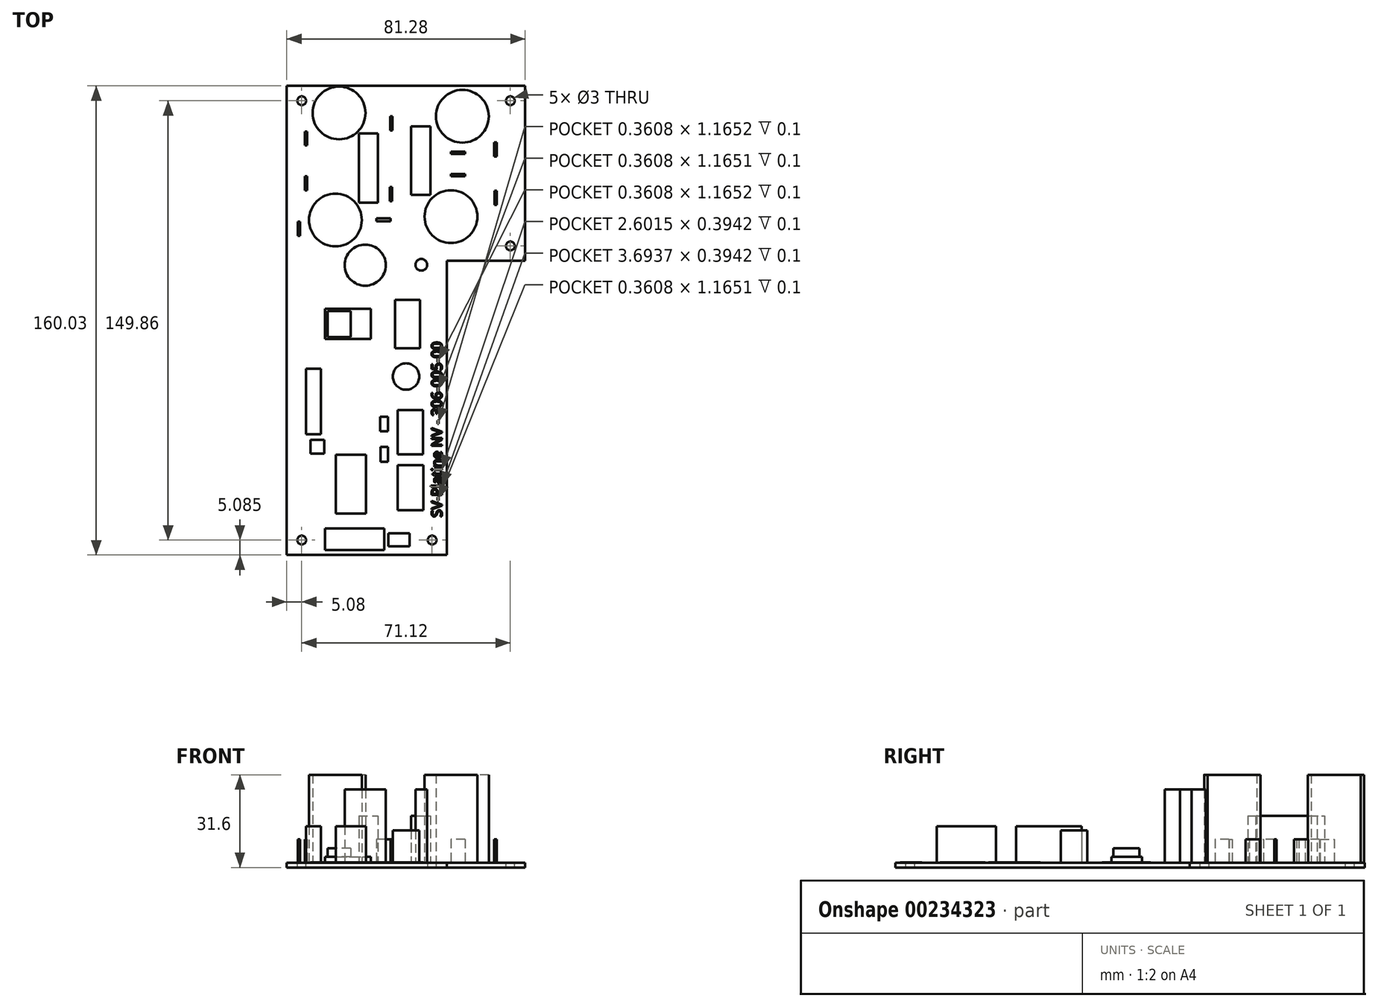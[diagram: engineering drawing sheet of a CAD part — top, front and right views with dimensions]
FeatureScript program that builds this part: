
annotation { "Feature Type Name" : "Feature", "Feature Type Description" : "" }
export const myFeature = defineFeature(function(context is Context, id is Id, definition is map)
    precondition{}
    {
        {
            var Q0;
            Q0=qCreatedBy(makeId("Top.planeOp"),FACE);
            var sketch = newSketch(context, id + "F0", { "sketchPlane" : qUnion([Q0])});
            skLineSegment(sketch, "E0.bottom", {"start": v(40.64, -29.84) * mm, "end": v(13.97, -29.84) * mm});
            skLineSegment(sketch, "E0.top", {"start": v(40.64, 29.85) * mm, "end": v(-40.64, 29.85) * mm});
            skLineSegment(sketch, "E0.left", {"start": v(40.64, -29.84) * mm, "end": v(40.64, 29.85) * mm});
            skLineSegment(sketch, "E0.right", {"start": v(-40.64, -29.84) * mm, "end": v(-40.64, 29.85) * mm});
            skPoint(sketch, "E0.middle", {"position": v(0, 0) * mm});
            skCircle(sketch, "E1.MirrorC", {"center": v(35.56, -24.76) * mm, "radius": 1.5 * mm});
            skCircle(sketch, "E2.MirrorC", {"center": v(-35.56, 24.77) * mm, "radius": 1.5 * mm});
            skCircle(sketch, "E3.MirrorC", {"center": v(35.56, 24.76) * mm, "radius": 1.5 * mm});
            skLineSegment(sketch, "E4.top", {"start": v(-40.64, -130.18) * mm, "end": v(13.97, -130.18) * mm});
            skLineSegment(sketch, "E4.left", {"start": v(-40.64, -29.84) * mm, "end": v(-40.64, -130.18) * mm});
            skLineSegment(sketch, "E4.right", {"start": v(13.97, -29.84) * mm, "end": v(13.97, -130.18) * mm});
            skCircle(sketch, "E5.MirrorC", {"center": v(-35.56, -125.1) * mm, "radius": 1.5 * mm});
            skCircle(sketch, "E6", {"center": v(8.89, -125.1) * mm, "radius": 1.5 * mm});
            skSolve(sketch);
        }
        {
            var Q0;
            Q0=makeQuery(id+"F0.imprint","IMPRINT",FACE,{"disambiguationData":[TD([[makeQuery(id+"F0.imprint","IMPRINT",EDGE,{"derivedFrom":sQuery(id+"F0.wireOp",EDGE,"Te7iasoo-ddtE-R7LS-BblS-gFD69E2wKtYx")}),-1.0]])]});
            var Q1;
            Q1=makeQuery(id+"F0.imprint","IMPRINT",FACE,{"disambiguationData":[TD([[makeQuery(id+"F0.imprint","IMPRINT",EDGE,{"derivedFrom":sQuery(id+"F0.wireOp",EDGE,"E4.bottom")}),-1.0]])]});
            var Q2;
            Q2=makeQuery(id+"F0.imprint","IMPRINT",FACE,{"disambiguationData":[TD([[makeQuery(id+"F0.imprint","IMPRINT",EDGE,{"derivedFrom":sQuery(id+"F0.wireOp",EDGE,"E0.bottom")}),-1.0]])]});
            extrude(context, id + "F1", {"entities" : qUnion([Q0, Q1, Q2]), "oppositeDirection" : true, "depth" : 1.6 * mm, "offsetDistance" : 25 * mm});
        }
        {
            var Q0;
            Q0=makeQuery(id+"F1.opExtrude","CAP_FACE",FACE,{"disambiguationData":[OSD([sQuery(id+"F0.wireOp",EDGE,"E0.bottom"),sQuery(id+"F0.wireOp",EDGE,"E0.top"),sQuery(id+"F0.wireOp",EDGE,"E0.left"),sQuery(id+"F0.wireOp",EDGE,"E0.right"),sQuery(id+"F0.wireOp",EDGE,"E1.MirrorC"),sQuery(id+"F0.wireOp",EDGE,"E2.MirrorC"),sQuery(id+"F0.wireOp",EDGE,"E3.MirrorC"),sQuery(id+"F0.wireOp",EDGE,"E4.top"),sQuery(id+"F0.wireOp",EDGE,"E4.left"),sQuery(id+"F0.wireOp",EDGE,"E4.right"),sQuery(id+"F0.wireOp",EDGE,"E5.MirrorC")])],"isStart":true});
            var sketch = newSketch(context, id + "F2", { "sketchPlane" : qUnion([Q0])});
            skText(sketch, "E7", { "text": "SV-Platine NV - 306-005-00", "fontName": "OpenSans-Regular.ttf"});
            const initialGuessF2  = {"E7": [0.0122, -0.11735, 0, 1, 0.0035]};
            skSetInitialGuess(sketch, initialGuessF2);
            skSolve(sketch);
        }
        {
            var Q0;
            Q0 = qSketchRegion(id + "F2", true);
            extrude(context, id + "F3", {"entities" : qUnion([Q0]), "operationType" : NewBodyOperationType.REMOVE, "oppositeDirection" : true, "depth" : .1 * mm, "offsetDistance" : 25 * mm});
        }
        {
            var Q0;
            {var subQ0=sQuery(id+"F0.wireOp",EDGE,"E4.right");var subQ1=sQuery(id+"F0.wireOp",EDGE,"E4.top");var subQ2=sQuery(id+"F0.wireOp",EDGE,"E3.MirrorC");var subQ3=sQuery(id+"F0.wireOp",EDGE,"E2.MirrorC");var subQ4=sQuery(id+"F0.wireOp",EDGE,"E1.MirrorC");var subQ5=sQuery(id+"F0.wireOp",EDGE,"E5.MirrorC");var subQ6=sQuery(id+"F0.wireOp",EDGE,"E0.bottom");var subQ7=sQuery(id+"F0.wireOp",EDGE,"E4.left");var subQ8=sQuery(id+"F0.wireOp",EDGE,"E0.right");var subQ9=sQuery(id+"F0.wireOp",EDGE,"E0.top");var subQ10=sQuery(id+"F0.wireOp",EDGE,"E0.left");var subQ11=sQuery(id+"F0.wireOp",EDGE,"E6");Q0=makeQuery(id+"F3.boolean.opBoolean","SPLIT",FACE,{"disambiguationData":[TD([makeQuery(id+"F1.opExtrude","SWEPT_FACE",FACE,{"disambiguationData":[OSD([subQ6])]})])],"derivedFrom":makeQuery(id+"F1.opExtrude","CAP_FACE",FACE,{"disambiguationData":[OSD([subQ6,subQ9,subQ10,subQ8,subQ4,subQ3,subQ2,subQ1,subQ7,subQ0,subQ5,subQ11])],"isStart":true})});}
            var sketch = newSketch(context, id + "F4", { "sketchPlane" : qUnion([Q0])});
            skCircle(sketch, "E8", {"center": v(-24.07, -15.93) * mm, "radius": 9 * mm});
            skCircle(sketch, "E9", {"center": v(-22.82, 20.6) * mm, "radius": 9 * mm});
            skCircle(sketch, "E10", {"center": v(15.31, -14.76) * mm, "radius": 9 * mm});
            skCircle(sketch, "E11", {"center": v(19.21, 19.47) * mm, "radius": 9 * mm});
            skCircle(sketch, "E12", {"center": v(-13.91, -31.32) * mm, "radius": 7 * mm});
            skCircle(sketch, "E13", {"center": v(-26.64, -61.49) * mm, "radius": 3 * mm});
            skCircle(sketch, "E14", {"center": v(0, -69.3) * mm, "radius": 4.5 * mm});
            skLineSegment(sketch, "E15.bottom", {"start": v(-27.68, -56.55) * mm, "end": v(-11.95, -56.55) * mm});
            skLineSegment(sketch, "E15.top", {"start": v(-27.68, -46.15) * mm, "end": v(-11.95, -46.15) * mm});
            skLineSegment(sketch, "E15.left", {"start": v(-27.68, -56.55) * mm, "end": v(-27.68, -46.15) * mm});
            skLineSegment(sketch, "E15.right", {"start": v(-11.95, -56.55) * mm, "end": v(-11.95, -46.15) * mm});
            skLineSegment(sketch, "E16.bottom", {"start": v(-18.88, -46.95) * mm, "end": v(-26.79, -46.95) * mm});
            skLineSegment(sketch, "E16.top", {"start": v(-18.88, -55.84) * mm, "end": v(-26.79, -55.84) * mm});
            skLineSegment(sketch, "E16.left", {"start": v(-18.88, -46.95) * mm, "end": v(-18.88, -55.84) * mm});
            skLineSegment(sketch, "E16.right", {"start": v(-26.79, -46.95) * mm, "end": v(-26.79, -55.84) * mm});
            skLineSegment(sketch, "E17.bottom", {"start": v(-3.71, -59.64) * mm, "end": v(4.76, -59.64) * mm});
            skLineSegment(sketch, "E17.top", {"start": v(-3.71, -43.2) * mm, "end": v(4.76, -43.2) * mm});
            skLineSegment(sketch, "E17.left", {"start": v(-3.71, -59.64) * mm, "end": v(-3.71, -43.2) * mm});
            skLineSegment(sketch, "E17.right", {"start": v(4.76, -59.64) * mm, "end": v(4.76, -43.2) * mm});
            skLineSegment(sketch, "E18.bottom", {"start": v(-2.88, -95.85) * mm, "end": v(5.83, -95.85) * mm});
            skLineSegment(sketch, "E18.top", {"start": v(-2.88, -80.74) * mm, "end": v(5.83, -80.74) * mm});
            skLineSegment(sketch, "E18.left", {"start": v(-2.88, -95.85) * mm, "end": v(-2.88, -80.74) * mm});
            skLineSegment(sketch, "E18.right", {"start": v(5.83, -95.85) * mm, "end": v(5.83, -80.74) * mm});
            skLineSegment(sketch, "E19.bottom", {"start": v(-2.88, -114.87) * mm, "end": v(5.92, -114.87) * mm});
            skLineSegment(sketch, "E19.top", {"start": v(-2.88, -99.58) * mm, "end": v(5.92, -99.58) * mm});
            skLineSegment(sketch, "E19.left", {"start": v(-2.88, -114.87) * mm, "end": v(-2.88, -99.58) * mm});
            skLineSegment(sketch, "E19.right", {"start": v(5.92, -114.87) * mm, "end": v(5.92, -99.58) * mm});
            skLineSegment(sketch, "E20.bottom", {"start": v(-27.68, -128.52) * mm, "end": v(-7.41, -128.52) * mm});
            skLineSegment(sketch, "E20.top", {"start": v(-27.68, -121.14) * mm, "end": v(-7.41, -121.14) * mm});
            skLineSegment(sketch, "E20.left", {"start": v(-27.68, -128.52) * mm, "end": v(-27.68, -121.14) * mm});
            skLineSegment(sketch, "E20.right", {"start": v(-7.41, -128.52) * mm, "end": v(-7.41, -121.14) * mm});
            skLineSegment(sketch, "E21.bottom", {"start": v(-6, -127.28) * mm, "end": v(1.2, -127.28) * mm});
            skLineSegment(sketch, "E21.top", {"start": v(-6, -122.74) * mm, "end": v(1.2, -122.74) * mm});
            skLineSegment(sketch, "E21.left", {"start": v(-6, -127.28) * mm, "end": v(-6, -122.74) * mm});
            skLineSegment(sketch, "E21.right", {"start": v(1.2, -127.28) * mm, "end": v(1.2, -122.74) * mm});
            skLineSegment(sketch, "E22.bottom", {"start": v(-34.04, -88.97) * mm, "end": v(-29.08, -88.97) * mm});
            skLineSegment(sketch, "E22.top", {"start": v(-34.04, -66.69) * mm, "end": v(-29.08, -66.69) * mm});
            skLineSegment(sketch, "E22.left", {"start": v(-34.04, -88.97) * mm, "end": v(-34.04, -66.69) * mm});
            skLineSegment(sketch, "E22.right", {"start": v(-29.08, -88.97) * mm, "end": v(-29.08, -66.69) * mm});
            skLineSegment(sketch, "E23.bottom", {"start": v(-23.94, -116.1) * mm, "end": v(-13.63, -116.1) * mm});
            skLineSegment(sketch, "E23.top", {"start": v(-23.94, -95.92) * mm, "end": v(-13.63, -95.92) * mm});
            skLineSegment(sketch, "E23.left", {"start": v(-23.94, -116.1) * mm, "end": v(-23.94, -95.92) * mm});
            skLineSegment(sketch, "E23.right", {"start": v(-13.63, -116.1) * mm, "end": v(-13.63, -95.92) * mm});
            skLineSegment(sketch, "E24.bottom", {"start": v(-8.75, -98.41) * mm, "end": v(-6.17, -98.41) * mm});
            skLineSegment(sketch, "E24.top", {"start": v(-8.75, -93.26) * mm, "end": v(-6.17, -93.26) * mm});
            skLineSegment(sketch, "E24.left", {"start": v(-8.75, -98.41) * mm, "end": v(-8.75, -93.26) * mm});
            skLineSegment(sketch, "E24.right", {"start": v(-6.17, -98.41) * mm, "end": v(-6.17, -93.26) * mm});
            skLineSegment(sketch, "E25.bottom", {"start": v(-8.76, -88.03) * mm, "end": v(-6.17, -88.03) * mm});
            skLineSegment(sketch, "E25.top", {"start": v(-8.76, -83.06) * mm, "end": v(-6.17, -83.06) * mm});
            skLineSegment(sketch, "E25.left", {"start": v(-8.76, -88.03) * mm, "end": v(-8.76, -83.06) * mm});
            skLineSegment(sketch, "E25.right", {"start": v(-6.17, -88.03) * mm, "end": v(-6.17, -83.06) * mm});
            skLineSegment(sketch, "E26.bottom", {"start": v(-16.12, -10.04) * mm, "end": v(-9.55, -10.04) * mm});
            skLineSegment(sketch, "E26.top", {"start": v(-16.12, 13.6) * mm, "end": v(-9.55, 13.6) * mm});
            skLineSegment(sketch, "E26.left", {"start": v(-16.12, -10.04) * mm, "end": v(-16.12, 13.6) * mm});
            skLineSegment(sketch, "E26.right", {"start": v(-9.55, -10.04) * mm, "end": v(-9.55, 13.6) * mm});
            skLineSegment(sketch, "E27.bottom", {"start": v(1.65, -7.38) * mm, "end": v(8.32, -7.38) * mm});
            skLineSegment(sketch, "E27.top", {"start": v(1.65, 16.09) * mm, "end": v(8.32, 16.09) * mm});
            skLineSegment(sketch, "E27.left", {"start": v(1.65, -7.38) * mm, "end": v(1.65, 16.09) * mm});
            skLineSegment(sketch, "E27.right", {"start": v(8.32, -7.38) * mm, "end": v(8.32, 16.09) * mm});
            skCircle(sketch, "E28", {"center": v(5.2, -31.2) * mm, "radius": 2 * mm});
            skLineSegment(sketch, "E29.bottom", {"start": v(-34.5, 14.31) * mm, "end": v(-33.7, 14.31) * mm});
            skLineSegment(sketch, "E29.top", {"start": v(-34.5, 9.51) * mm, "end": v(-33.7, 9.51) * mm});
            skLineSegment(sketch, "E29.left", {"start": v(-34.5, 14.31) * mm, "end": v(-34.5, 9.51) * mm});
            skLineSegment(sketch, "E29.right", {"start": v(-33.7, 14.31) * mm, "end": v(-33.7, 9.51) * mm});
            skLineSegment(sketch, "E30.bottom", {"start": v(-34.5, -0.96) * mm, "end": v(-33.7, -0.96) * mm});
            skLineSegment(sketch, "E30.top", {"start": v(-34.5, -5.76) * mm, "end": v(-33.7, -5.76) * mm});
            skLineSegment(sketch, "E30.left", {"start": v(-34.5, -0.96) * mm, "end": v(-34.5, -5.76) * mm});
            skLineSegment(sketch, "E30.right", {"start": v(-33.7, -0.96) * mm, "end": v(-33.7, -5.76) * mm});
            skLineSegment(sketch, "E31.bottom", {"start": v(-36.9, -16.45) * mm, "end": v(-36.1, -16.45) * mm});
            skLineSegment(sketch, "E31.top", {"start": v(-36.9, -21.25) * mm, "end": v(-36.1, -21.25) * mm});
            skLineSegment(sketch, "E31.left", {"start": v(-36.9, -16.45) * mm, "end": v(-36.9, -21.25) * mm});
            skLineSegment(sketch, "E31.right", {"start": v(-36.1, -16.45) * mm, "end": v(-36.1, -21.25) * mm});
            skLineSegment(sketch, "E32.bottom", {"start": v(-32.58, -90.9) * mm, "end": v(-27.92, -90.9) * mm});
            skLineSegment(sketch, "E32.top", {"start": v(-32.58, -95.62) * mm, "end": v(-27.92, -95.62) * mm});
            skLineSegment(sketch, "E32.left", {"start": v(-32.58, -90.9) * mm, "end": v(-32.58, -95.62) * mm});
            skLineSegment(sketch, "E32.right", {"start": v(-27.92, -90.9) * mm, "end": v(-27.92, -95.62) * mm});
            skLineSegment(sketch, "E33.bottom", {"start": v(-4.64, 14.65) * mm, "end": v(-5.44, 14.65) * mm});
            skLineSegment(sketch, "E33.top", {"start": v(-4.64, 19.45) * mm, "end": v(-5.44, 19.45) * mm});
            skLineSegment(sketch, "E33.left", {"start": v(-4.64, 14.65) * mm, "end": v(-4.64, 19.45) * mm});
            skLineSegment(sketch, "E33.right", {"start": v(-5.44, 14.65) * mm, "end": v(-5.44, 19.45) * mm});
            skPoint(sketch, "E33.middle", {"position": v(-5.04, 17.05) * mm});
            skLineSegment(sketch, "E34.bottom", {"start": v(-4.71, -9.51) * mm, "end": v(-5.51, -9.51) * mm});
            skLineSegment(sketch, "E34.top", {"start": v(-4.71, -4.71) * mm, "end": v(-5.51, -4.71) * mm});
            skLineSegment(sketch, "E34.left", {"start": v(-4.71, -9.51) * mm, "end": v(-4.71, -4.71) * mm});
            skLineSegment(sketch, "E34.right", {"start": v(-5.51, -9.51) * mm, "end": v(-5.51, -4.71) * mm});
            skPoint(sketch, "E34.middle", {"position": v(-5.11, -7.11) * mm});
            skLineSegment(sketch, "E35.bottom", {"start": v(-5.28, -16.42) * mm, "end": v(-10.08, -16.42) * mm});
            skLineSegment(sketch, "E35.top", {"start": v(-5.28, -15.37) * mm, "end": v(-10.08, -15.37) * mm});
            skLineSegment(sketch, "E35.left", {"start": v(-5.28, -16.42) * mm, "end": v(-5.28, -15.37) * mm});
            skLineSegment(sketch, "E35.right", {"start": v(-10.08, -16.42) * mm, "end": v(-10.08, -15.37) * mm});
            skPoint(sketch, "E35.middle", {"position": v(-7.68, -15.9) * mm});
            skLineSegment(sketch, "E36.bottom", {"start": v(20.16, -1.01) * mm, "end": v(15.36, -1.01) * mm});
            skLineSegment(sketch, "E36.top", {"start": v(20.16, -0.21) * mm, "end": v(15.36, -0.21) * mm});
            skLineSegment(sketch, "E36.left", {"start": v(20.16, -1.01) * mm, "end": v(20.16, -0.21) * mm});
            skLineSegment(sketch, "E36.right", {"start": v(15.36, -1.01) * mm, "end": v(15.36, -0.21) * mm});
            skPoint(sketch, "E36.middle", {"position": v(17.76, -0.61) * mm});
            skLineSegment(sketch, "E37.bottom", {"start": v(20.1, 6.57) * mm, "end": v(15.3, 6.57) * mm});
            skLineSegment(sketch, "E37.top", {"start": v(20.1, 7.37) * mm, "end": v(15.3, 7.37) * mm});
            skLineSegment(sketch, "E37.left", {"start": v(20.1, 6.57) * mm, "end": v(20.1, 7.37) * mm});
            skLineSegment(sketch, "E37.right", {"start": v(15.3, 6.57) * mm, "end": v(15.3, 7.37) * mm});
            skPoint(sketch, "E37.middle", {"position": v(17.7, 6.97) * mm});
            skLineSegment(sketch, "E38.bottom", {"start": v(30.87, 5.76) * mm, "end": v(30.07, 5.76) * mm});
            skLineSegment(sketch, "E38.top", {"start": v(30.87, 10.56) * mm, "end": v(30.07, 10.56) * mm});
            skLineSegment(sketch, "E38.left", {"start": v(30.87, 5.76) * mm, "end": v(30.87, 10.56) * mm});
            skLineSegment(sketch, "E38.right", {"start": v(30.07, 5.76) * mm, "end": v(30.07, 10.56) * mm});
            skPoint(sketch, "E38.middle", {"position": v(30.47, 8.16) * mm});
            skLineSegment(sketch, "E39.bottom", {"start": v(30.9, -10.75) * mm, "end": v(30.1, -10.75) * mm});
            skLineSegment(sketch, "E39.top", {"start": v(30.9, -5.95) * mm, "end": v(30.1, -5.95) * mm});
            skLineSegment(sketch, "E39.left", {"start": v(30.9, -10.75) * mm, "end": v(30.9, -5.95) * mm});
            skLineSegment(sketch, "E39.right", {"start": v(30.1, -10.75) * mm, "end": v(30.1, -5.95) * mm});
            skPoint(sketch, "E39.middle", {"position": v(30.5, -8.35) * mm});
            skSolve(sketch);
        }
        {
            var Q0;
            Q0=makeQuery(id+"F4.imprint","IMPRINT",FACE,{"disambiguationData":[TD([[makeQuery(id+"F4.imprint","IMPRINT",EDGE,{"derivedFrom":sQuery(id+"F4.wireOp",EDGE,"E11")}),1.0]])]});
            var Q1;
            Q1=makeQuery(id+"F4.imprint","IMPRINT",FACE,{"disambiguationData":[TD([[makeQuery(id+"F4.imprint","IMPRINT",EDGE,{"derivedFrom":sQuery(id+"F4.wireOp",EDGE,"E9")}),1.0]])]});
            var Q2;
            Q2=makeQuery(id+"F4.imprint","IMPRINT",FACE,{"disambiguationData":[TD([[makeQuery(id+"F4.imprint","IMPRINT",EDGE,{"derivedFrom":sQuery(id+"F4.wireOp",EDGE,"E8")}),1.0]])]});
            var Q3;
            Q3=makeQuery(id+"F4.imprint","IMPRINT",FACE,{"disambiguationData":[TD([[makeQuery(id+"F4.imprint","IMPRINT",EDGE,{"derivedFrom":sQuery(id+"F4.wireOp",EDGE,"E10")}),1.0]])]});
            extrude(context, id + "F5", {"entities" : qUnion([Q0, Q1, Q2, Q3]), "operationType" : NewBodyOperationType.ADD, "depth" : 30 * mm, "offsetDistance" : 25 * mm});
        }
        {
            var Q0;
            Q0=makeQuery(id+"F4.imprint","IMPRINT",FACE,{"disambiguationData":[TD([[makeQuery(id+"F4.imprint","IMPRINT",EDGE,{"derivedFrom":sQuery(id+"F4.wireOp",EDGE,"E12")}),1.0]])]});
            extrude(context, id + "F6", {"entities" : qUnion([Q0]), "operationType" : NewBodyOperationType.ADD, "depth" : 25 * mm, "offsetDistance" : 25 * mm});
        }
        {
            var Q0;
            Q0=makeQuery(id+"F4.imprint","IMPRINT",FACE,{"disambiguationData":[TD([[makeQuery(id+"F4.imprint","IMPRINT",EDGE,{"derivedFrom":sQuery(id+"F4.wireOp",EDGE,"E27.bottom")}),1.0]])]});
            var Q1;
            Q1=makeQuery(id+"F4.imprint","IMPRINT",FACE,{"disambiguationData":[TD([[makeQuery(id+"F4.imprint","IMPRINT",EDGE,{"derivedFrom":sQuery(id+"F4.wireOp",EDGE,"E26.bottom")}),1.0]])]});
            extrude(context, id + "F7", {"entities" : qUnion([Q0, Q1]), "operationType" : NewBodyOperationType.ADD, "depth" : 16 * mm, "offsetDistance" : 25 * mm});
        }
        {
            var Q0;
            Q0=makeQuery(id+"F4.imprint","IMPRINT",FACE,{"disambiguationData":[TD([[makeQuery(id+"F4.imprint","IMPRINT",EDGE,{"derivedFrom":sQuery(id+"F4.wireOp",EDGE,"E29.bottom")}),-1.0]])]});
            var Q1;
            Q1=makeQuery(id+"F4.imprint","IMPRINT",FACE,{"disambiguationData":[TD([[makeQuery(id+"F4.imprint","IMPRINT",EDGE,{"derivedFrom":sQuery(id+"F4.wireOp",EDGE,"E30.bottom")}),-1.0]])]});
            var Q2;
            Q2=makeQuery(id+"F4.imprint","IMPRINT",FACE,{"disambiguationData":[TD([[makeQuery(id+"F4.imprint","IMPRINT",EDGE,{"derivedFrom":sQuery(id+"F4.wireOp",EDGE,"E31.bottom")}),-1.0]])]});
            var Q3;
            Q3=makeQuery(id+"F4.imprint","IMPRINT",FACE,{"disambiguationData":[TD([[makeQuery(id+"F4.imprint","IMPRINT",EDGE,{"derivedFrom":sQuery(id+"F4.wireOp",EDGE,"E34.bottom")}),-1.0]])]});
            var Q4;
            Q4=makeQuery(id+"F4.imprint","IMPRINT",FACE,{"disambiguationData":[TD([[makeQuery(id+"F4.imprint","IMPRINT",EDGE,{"derivedFrom":sQuery(id+"F4.wireOp",EDGE,"E35.bottom")}),-1.0]])]});
            var Q5;
            Q5=makeQuery(id+"F4.imprint","IMPRINT",FACE,{"disambiguationData":[TD([[makeQuery(id+"F4.imprint","IMPRINT",EDGE,{"derivedFrom":sQuery(id+"F4.wireOp",EDGE,"E36.bottom")}),-1.0]])]});
            var Q6;
            Q6=makeQuery(id+"F4.imprint","IMPRINT",FACE,{"disambiguationData":[TD([[makeQuery(id+"F4.imprint","IMPRINT",EDGE,{"derivedFrom":sQuery(id+"F4.wireOp",EDGE,"E39.bottom")}),-1.0]])]});
            var Q7;
            Q7=makeQuery(id+"F4.imprint","IMPRINT",FACE,{"disambiguationData":[TD([[makeQuery(id+"F4.imprint","IMPRINT",EDGE,{"derivedFrom":sQuery(id+"F4.wireOp",EDGE,"E37.bottom")}),-1.0]])]});
            var Q8;
            Q8=makeQuery(id+"F4.imprint","IMPRINT",FACE,{"disambiguationData":[TD([[makeQuery(id+"F4.imprint","IMPRINT",EDGE,{"derivedFrom":sQuery(id+"F4.wireOp",EDGE,"E38.bottom")}),-1.0]])]});
            var Q9;
            Q9=makeQuery(id+"F4.imprint","IMPRINT",FACE,{"disambiguationData":[TD([[makeQuery(id+"F4.imprint","IMPRINT",EDGE,{"derivedFrom":sQuery(id+"F4.wireOp",EDGE,"E33.bottom")}),-1.0]])]});
            extrude(context, id + "F8", {"entities" : qUnion([Q0, Q1, Q2, Q3, Q4, Q5, Q6, Q7, Q8, Q9]), "operationType" : NewBodyOperationType.ADD, "depth" : 8 * mm, "offsetDistance" : 25 * mm});
        }
        {
            var Q0;
            Q0=makeQuery(id+"F4.imprint","IMPRINT",FACE,{"disambiguationData":[TD([[makeQuery(id+"F4.imprint","IMPRINT",EDGE,{"derivedFrom":sQuery(id+"F4.wireOp",EDGE,"E22.bottom")}),1.0]])]});
            var Q1;
            Q1=makeQuery(id+"F4.imprint","IMPRINT",FACE,{"disambiguationData":[TD([[makeQuery(id+"F4.imprint","IMPRINT",EDGE,{"derivedFrom":sQuery(id+"F4.wireOp",EDGE,"E23.bottom")}),1.0]])]});
            extrude(context, id + "F9", {"entities" : qUnion([Q0, Q1]), "operationType" : NewBodyOperationType.ADD, "depth" : 12.5 * mm, "offsetDistance" : 25 * mm});
        }
        {
            var Q0;
            Q0=makeQuery(id+"F4.imprint","IMPRINT",FACE,{"disambiguationData":[TD([[makeQuery(id+"F4.imprint","IMPRINT",EDGE,{"derivedFrom":sQuery(id+"F4.wireOp",EDGE,"E14")}),1.0]])]});
            extrude(context, id + "F10", {"entities" : qUnion([Q0]), "operationType" : NewBodyOperationType.ADD, "depth" : 11 * mm, "offsetDistance" : 25 * mm});
        }
        {
            var Q0;
            Q0=makeQuery(id+"F4.imprint","IMPRINT",FACE,{"disambiguationData":[TD([[makeQuery(id+"F4.imprint","IMPRINT",EDGE,{"derivedFrom":sQuery(id+"F4.wireOp",EDGE,"E28")}),1.0]])]});
            extrude(context, id + "F11", {"entities" : qUnion([Q0]), "operationType" : NewBodyOperationType.ADD, "depth" : 25 * mm, "offsetDistance" : 25 * mm});
        }
        {
            var Q0;
            Q0=makeQuery(id+"F4.imprint","IMPRINT",FACE,{"disambiguationData":[TD([[makeQuery(id+"F4.imprint","IMPRINT",EDGE,{"derivedFrom":sQuery(id+"F4.wireOp",EDGE,"E16.bottom")}),1.0]])]});
            extrude(context, id + "F12", {"entities" : qUnion([Q0]), "operationType" : NewBodyOperationType.ADD, "depth" : 5 * mm, "offsetDistance" : 25 * mm});
        }
        {
            var Q0;
            Q0=makeQuery(id+"F4.imprint","IMPRINT",FACE,{"disambiguationData":[TD([[makeQuery(id+"F4.imprint","IMPRINT",EDGE,{"derivedFrom":sQuery(id+"F4.wireOp",EDGE,"E15.bottom")}),1.0]])]});
            extrude(context, id + "F13", {"entities" : qUnion([Q0]), "operationType" : NewBodyOperationType.ADD, "depth" : 2 * mm, "offsetDistance" : 25 * mm});
        }
        {
            var Q0;
            Q0=makeQuery(id+"F4.imprint","IMPRINT",FACE,{"disambiguationData":[TD([[makeQuery(id+"F4.imprint","IMPRINT",EDGE,{"derivedFrom":sQuery(id+"F4.wireOp",EDGE,"E19.bottom")}),1.0]])]});
            var Q1;
            Q1=makeQuery(id+"F4.imprint","IMPRINT",FACE,{"disambiguationData":[TD([[makeQuery(id+"F4.imprint","IMPRINT",EDGE,{"derivedFrom":sQuery(id+"F4.wireOp",EDGE,"E18.bottom")}),1.0]])]});
            var Q2;
            Q2=makeQuery(id+"F4.imprint","IMPRINT",FACE,{"disambiguationData":[TD([[makeQuery(id+"F4.imprint","IMPRINT",EDGE,{"derivedFrom":sQuery(id+"F4.wireOp",EDGE,"E21.bottom")}),1.0]])]});
            var Q3;
            Q3=makeQuery(id+"F4.imprint","IMPRINT",FACE,{"disambiguationData":[TD([[makeQuery(id+"F4.imprint","IMPRINT",EDGE,{"derivedFrom":sQuery(id+"F4.wireOp",EDGE,"E20.bottom")}),1.0]])]});
            var Q4;
            Q4=makeQuery(id+"F4.imprint","IMPRINT",FACE,{"disambiguationData":[TD([[makeQuery(id+"F4.imprint","IMPRINT",EDGE,{"derivedFrom":sQuery(id+"F4.wireOp",EDGE,"E17.bottom")}),1.0]])]});
            var Q5;
            Q5=makeQuery(id+"F4.imprint","IMPRINT",FACE,{"disambiguationData":[TD([[makeQuery(id+"F4.imprint","IMPRINT",EDGE,{"derivedFrom":sQuery(id+"F4.wireOp",EDGE,"E32.bottom")}),-1.0]])]});
            var Q6;
            Q6=makeQuery(id+"F4.imprint","IMPRINT",FACE,{"disambiguationData":[TD([[makeQuery(id+"F4.imprint","IMPRINT",EDGE,{"derivedFrom":sQuery(id+"F4.wireOp",EDGE,"E24.bottom")}),1.0]])]});
            var Q7;
            Q7=makeQuery(id+"F4.imprint","IMPRINT",FACE,{"disambiguationData":[TD([[makeQuery(id+"F4.imprint","IMPRINT",EDGE,{"derivedFrom":sQuery(id+"F4.wireOp",EDGE,"E25.bottom")}),1.0]])]});
            var Q8;
            Q8=sQuery(id+"F4.wireOp",EDGE,"E19.bottom");
            var Q9;
            Q9=sQuery(id+"F4.wireOp",EDGE,"E19.right");
            var Q10;
            Q10=sQuery(id+"F4.wireOp",EDGE,"E19.top");
            var Q11;
            Q11=sQuery(id+"F4.wireOp",EDGE,"E19.left");
            extrude(context, id + "F14", {"entities" : qUnion([Q0, Q1, Q2, Q3, Q4, Q5, Q6, Q7]), "operationType" : NewBodyOperationType.ADD, "surfaceEntities" : qUnion([Q8, Q9, Q10, Q11]), "depth" : .1 * mm, "offsetDistance" : 25 * mm});
        }
    });
